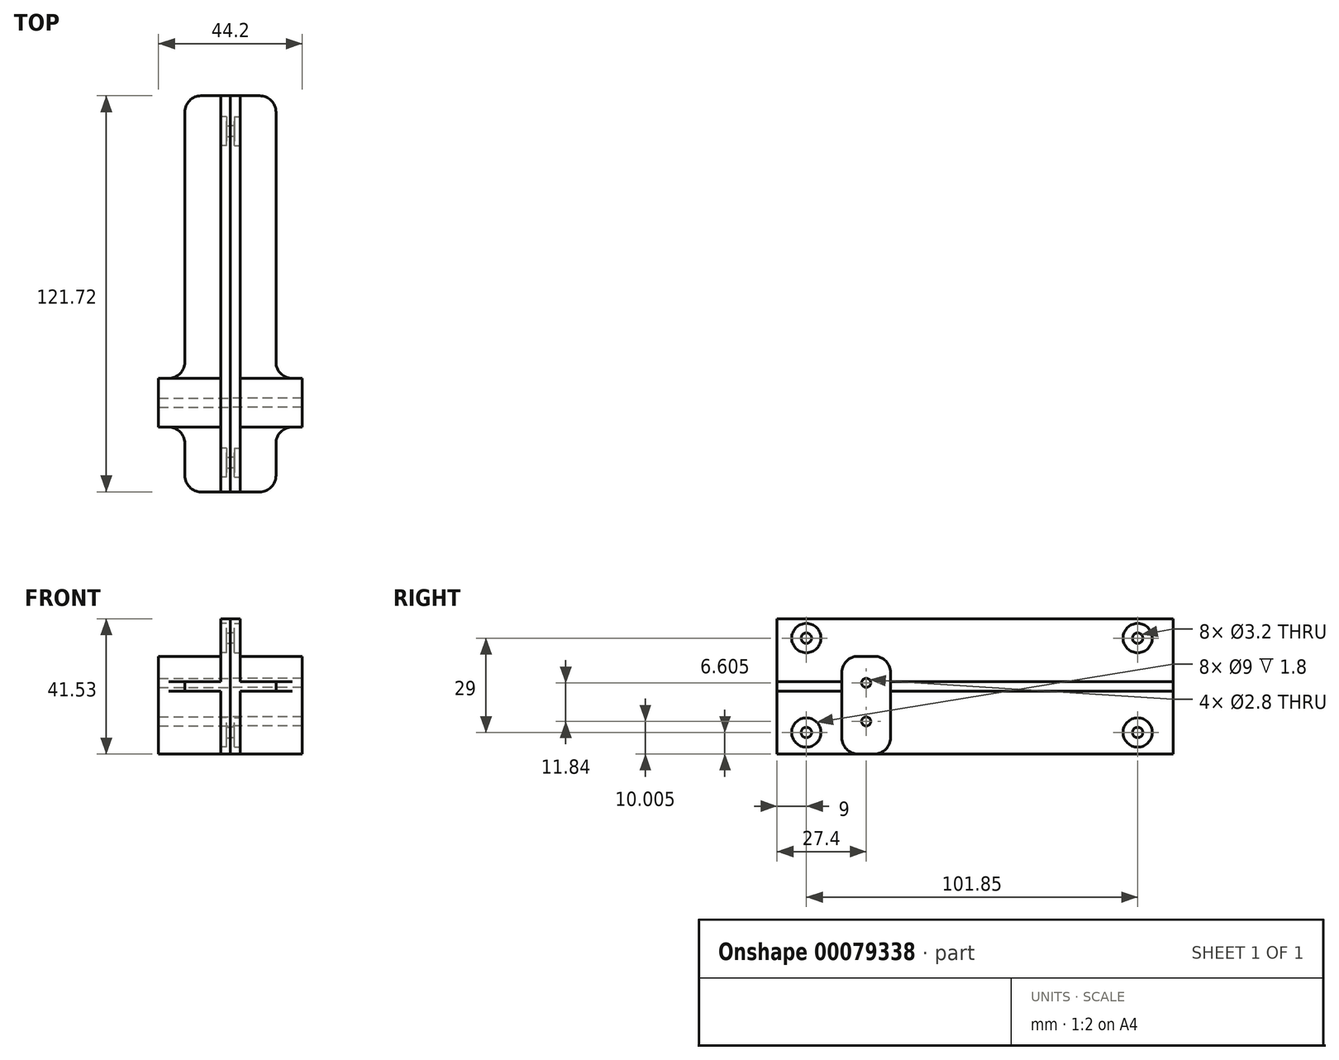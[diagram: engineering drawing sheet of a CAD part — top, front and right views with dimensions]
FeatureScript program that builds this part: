
annotation { "Feature Type Name" : "Feature", "Feature Type Description" : "" }
export const myFeature = defineFeature(function(context is Context, id is Id, definition is map)
    precondition{}
    {
        {
            var Q0;
            Q0=qCreatedBy(makeId("Right.planeOp"),FACE);
            var sketch = newSketch(context, id + "F0", { "sketchPlane" : qUnion([Q0])});
            skLineSegment(sketch, "E0.bottom", {"start": v(-83.36, 20.77) * mm, "end": v(83.36, 20.77) * mm});
            skLineSegment(sketch, "E0.top", {"start": v(-83.36, -20.76) * mm, "end": v(83.36, -20.76) * mm});
            skLineSegment(sketch, "E0.left", {"start": v(-83.36, 20.77) * mm, "end": v(-83.36, -20.76) * mm});
            skLineSegment(sketch, "E0.right", {"start": v(83.36, 20.77) * mm, "end": v(83.36, -20.76) * mm});
            skPoint(sketch, "E0.middle", {"position": v(0, 0) * mm});
            skLineSegment(sketch, "E1", {"start": v(-83.36, -10.77) * mm, "end": v(-35.96, -10.77) * mm, "construction": true});
            skLineSegment(sketch, "E2", {"start": v(-35.96, -10.76) * mm, "end": v(-35.96, -20.76) * mm, "construction": true});
            skLineSegment(sketch, "E3", {"start": v(-35.96, -10.77) * mm, "end": v(43.29, -10.77) * mm, "construction": true});
            skLineSegment(sketch, "E4", {"start": v(-35.96, -20.76) * mm, "end": v(-35.96, 1.08) * mm, "construction": true});
            skCircle(sketch, "E5", {"center": v(-35.96, -10.77) * mm, "radius": 1.4 * mm});
            skCircle(sketch, "E6", {"center": v(43.29, -10.77) * mm, "radius": 1.4 * mm});
            skCircle(sketch, "E7", {"center": v(-35.96, 1.08) * mm, "radius": 1.4 * mm});
            skLineSegment(sketch, "E8", {"start": v(-83.36, -14.16) * mm, "end": v(-54.36, -14.16) * mm, "construction": true});
            skLineSegment(sketch, "E9", {"start": v(-54.36, -14.16) * mm, "end": v(-54.36, -20.76) * mm, "construction": true});
            skLineSegment(sketch, "E10", {"start": v(-54.36, -14.16) * mm, "end": v(47.49, -14.16) * mm, "construction": true});
            skCircle(sketch, "E11", {"center": v(47.49, -14.16) * mm, "radius": 1.6 * mm});
            skCircle(sketch, "E12", {"center": v(-54.36, -14.16) * mm, "radius": 1.6 * mm});
            skLineSegment(sketch, "E13.bottom", {"start": v(-28.46, -20.76) * mm, "end": v(-43.46, -20.76) * mm});
            skLineSegment(sketch, "E13.left", {"start": v(-28.46, -20.76) * mm, "end": v(-28.46, 9.23) * mm});
            skLineSegment(sketch, "E13.right", {"start": v(-43.46, -20.76) * mm, "end": v(-43.46, 9.23) * mm});
            skLineSegment(sketch, "E14", {"start": v(-43.46, 9.23) * mm, "end": v(-28.46, 9.23) * mm});
            skLineSegment(sketch, "E15", {"start": v(-28.46, -5.76) * mm, "end": v(53.54, -5.76) * mm});
            skPoint(sketch, "E15.endSnap0", {"position": v(-28.46, -5.76) * mm});
            skLineSegment(sketch, "E16", {"start": v(53.54, -5.76) * mm, "end": v(53.54, -20.76) * mm});
            skLineSegment(sketch, "E17", {"start": v(-54.36, -14.16) * mm, "end": v(-54.36, 14.84) * mm, "construction": true});
            skLineSegment(sketch, "E18", {"start": v(-54.36, 14.84) * mm, "end": v(47.49, 14.84) * mm, "construction": true});
            skLineSegment(sketch, "E19", {"start": v(47.49, 14.84) * mm, "end": v(47.49, -14.16) * mm, "construction": true});
            skCircle(sketch, "E20", {"center": v(-54.36, 14.84) * mm, "radius": 1.6 * mm});
            skCircle(sketch, "E21", {"center": v(47.49, 14.84) * mm, "radius": 1.6 * mm});
            skSolve(sketch);
        }
        {
            var Q0;
            Q0=makeQuery(id+"F0.imprint","IMPRINT",FACE,{"disambiguationData":[TD([[makeQuery(id+"F0.imprint","IMPRINT",EDGE,{"derivedFrom":sQuery(id+"F0.wireOp",EDGE,"E0.bottom")}),-1.0]])]});
            var Q1;
            Q1=makeQuery(id+"F0.imprint","IMPRINT",FACE,{"disambiguationData":[TD([[makeQuery(id+"F0.imprint","IMPRINT",EDGE,{"derivedFrom":sQuery(id+"F0.wireOp",EDGE,"E6")}),-1.0]])]});
            var Q2;
            Q2=makeQuery(id+"F0.imprint","IMPRINT",FACE,{"disambiguationData":[TD([[makeQuery(id+"F0.imprint","IMPRINT",EDGE,{"derivedFrom":sQuery(id+"F0.wireOp",EDGE,"E6")}),1.0]])]});
            extrude(context, id + "F1", {"entities" : qUnion([Q0, Q1, Q2]), "depth" : 3 * mm});
        }
        {
            var Q0;
            Q0=makeQuery(id+"F0.imprint","IMPRINT",FACE,{"disambiguationData":[TD([[makeQuery(id+"F0.imprint","IMPRINT",EDGE,{"derivedFrom":sQuery(id+"F0.wireOp",EDGE,"E5")}),-1.0]])]});
            extrude(context, id + "F2", {"entities" : qUnion([Q0]), "operationType" : NewBodyOperationType.ADD, "depth" : 22.1 * mm});
        }
        {
            var Q0;
            Q0=makeQuery(id+"F2.opExtrude","SWEPT_EDGE",EDGE,{"disambiguationData":[OSD([sQuery(id+"F0.wireOp",EDGE,"E13.right"),sQuery(id+"F0.wireOp",EDGE,"E14")])]});
            var Q1;
            Q1=makeQuery(id+"F2.opExtrude","SWEPT_EDGE",EDGE,{"disambiguationData":[OSD([sQuery(id+"F0.wireOp",EDGE,"E13.left"),sQuery(id+"F0.wireOp",EDGE,"E14")])]});
            var Q2;
            Q2=makeQuery(id+"F2.opExtrude","SWEPT_EDGE",EDGE,{"disambiguationData":[OSD([sQuery(id+"F0.wireOp",EDGE,"E0.top"),sQuery(id+"F0.wireOp",EDGE,"E13.bottom"),sQuery(id+"F0.wireOp",EDGE,"E13.left")])]});
            var Q3;
            Q3=makeQuery(id+"F2.opExtrude","SWEPT_EDGE",EDGE,{"disambiguationData":[OSD([sQuery(id+"F0.wireOp",EDGE,"E0.top"),sQuery(id+"F0.wireOp",EDGE,"E13.bottom"),sQuery(id+"F0.wireOp",EDGE,"E13.right")])]});
            fillet(context, id + "F3", {"entities" : qUnion([Q0, Q1, Q2, Q3]), "radius" : 5 * mm, "tangentPropagation" : true, "allowEdgeOverflow" : false});
        }
        {
            var Q0;
            Q0=makeQuery(id+"F1.opExtrude","SWEPT_FACE",FACE,{"disambiguationData":[OSD([sQuery(id+"F0.wireOp",EDGE,"E0.left")])]});
            extrude(context, id + "F4", {"entities" : qUnion([Q0]), "operationType" : NewBodyOperationType.REMOVE, "oppositeDirection" : true, "depth" : 20 * mm});
        }
        {
            var Q0;
            Q0=makeQuery(id+"F1.opExtrude","SWEPT_FACE",FACE,{"disambiguationData":[OSD([sQuery(id+"F0.wireOp",EDGE,"E0.right")])]});
            extrude(context, id + "F5", {"entities" : qUnion([Q0]), "operationType" : NewBodyOperationType.REMOVE, "oppositeDirection" : true, "depth" : 25 * mm});
        }
        {
            var Q0;
            Q0=makeQuery(id+"F4.boolean.opBoolean","COPY",FACE,{"derivedFrom":makeQuery(id+"F4.opExtrude","CAP_FACE",FACE,{"disambiguationData":[OSD([sQuery(id+"F0.wireOp",EDGE,"E0.left")])],"isStart":false})});
            var sketch = newSketch(context, id + "F6", { "sketchPlane" : qUnion([Q0])});
            skLineSegment(sketch, "E22", {"start": v(3, 0) * mm, "end": v(3, 1.5) * mm});
            skLineSegment(sketch, "E23", {"start": v(3, 1.5) * mm, "end": v(14, 1.5) * mm});
            skLineSegment(sketch, "E24", {"start": v(14, 1.5) * mm, "end": v(14, -1.5) * mm});
            skLineSegment(sketch, "E25", {"start": v(14, -1.5) * mm, "end": v(3, -1.5) * mm});
            skLineSegment(sketch, "E26", {"start": v(3, -1.5) * mm, "end": v(3, 0) * mm});
            skSolve(sketch);
        }
        {
            var Q0;
            Q0=makeQuery(id+"F6.imprint","IMPRINT",FACE,{"disambiguationData":[TD([[makeQuery(id+"F6.imprint","IMPRINT",EDGE,{"derivedFrom":sQuery(id+"F6.wireOp",EDGE,"E22")}),1.0]])]});
            var Q1;
            Q1=makeQuery(id+"F5.boolean.opBoolean","COPY",FACE,{"derivedFrom":makeQuery(id+"F5.opExtrude","CAP_FACE",FACE,{"disambiguationData":[OSD([sQuery(id+"F0.wireOp",EDGE,"E0.right")])],"isStart":false})});
            extrude(context, id + "F7", {"entities" : qUnion([Q0]), "operationType" : NewBodyOperationType.ADD, "endBound" : BoundingType.UP_TO_SURFACE, "oppositeDirection" : true, "endBoundEntityFace" : qUnion([Q1]), "depth" : 25 * mm});
        }
        {
            var Q0;
            Q0=makeQuery(id+"F4.boolean.opBoolean","COPY",EDGE,{"derivedFrom":makeQuery(id+"F4.opExtrude","CAP_EDGE",EDGE,{"disambiguationData":[OSD([sQuery(id+"F0.wireOp",EDGE,"E0.top"),sQuery(id+"F0.wireOp",EDGE,"E0.left")])],"isStart":false})});
            var Q1;
            Q1=makeQuery(id+"F5.boolean.opBoolean","COPY",EDGE,{"derivedFrom":makeQuery(id+"F5.opExtrude","CAP_EDGE",EDGE,{"disambiguationData":[OSD([sQuery(id+"F0.wireOp",EDGE,"E0.top"),sQuery(id+"F0.wireOp",EDGE,"E0.right")])],"isStart":false})});
            var Q2;
            Q2=makeQuery(id+"F7.opExtrude","CAP_EDGE",EDGE,{"disambiguationData":[OSD([sQuery(id+"F6.wireOp",EDGE,"E24")])],"isStart":false});
            var Q3;
            Q3=makeQuery(id+"F7.boolean.opBoolean","INTERSECT",EDGE,{"derivedFrom":[makeQuery(id+"F2.opExtrude","SWEPT_FACE",FACE,{"disambiguationData":[OSD([sQuery(id+"F0.wireOp",EDGE,"E13.left")])]}),makeQuery(id+"F7.opExtrude","SWEPT_FACE",FACE,{"disambiguationData":[OSD([sQuery(id+"F6.wireOp",EDGE,"E24")])]})]});
            var Q4;
            Q4=makeQuery(id+"F7.boolean.opBoolean","INTERSECT",EDGE,{"derivedFrom":[makeQuery(id+"F2.opExtrude","SWEPT_FACE",FACE,{"disambiguationData":[OSD([sQuery(id+"F0.wireOp",EDGE,"E13.right")])]}),makeQuery(id+"F7.opExtrude","SWEPT_FACE",FACE,{"disambiguationData":[OSD([sQuery(id+"F6.wireOp",EDGE,"E24")])]})]});
            var Q5;
            Q5=makeQuery(id+"F7.opExtrude","CAP_EDGE",EDGE,{"disambiguationData":[OSD([sQuery(id+"F6.wireOp",EDGE,"E24")])],"isStart":true});
            var Q6;
            Q6=makeQuery(id+"F4.boolean.opBoolean","COPY",EDGE,{"derivedFrom":makeQuery(id+"F4.opExtrude","CAP_EDGE",EDGE,{"disambiguationData":[OSD([sQuery(id+"F0.wireOp",EDGE,"E0.bottom"),sQuery(id+"F0.wireOp",EDGE,"E0.left")])],"isStart":false})});
            var Q7;
            Q7=makeQuery(id+"F5.boolean.opBoolean","COPY",EDGE,{"derivedFrom":makeQuery(id+"F5.opExtrude","CAP_EDGE",EDGE,{"disambiguationData":[OSD([sQuery(id+"F0.wireOp",EDGE,"E0.bottom"),sQuery(id+"F0.wireOp",EDGE,"E0.right")])],"isStart":false})});
            fillet(context, id + "F8", {"entities" : qUnion([Q0, Q1, Q2, Q3, Q4, Q5, Q6, Q7]), "radius" : 5 * mm, "tangentPropagation" : true, "allowEdgeOverflow" : false});
        }
        {
            var Q0;
            {var subQ2=sQuery(id+"F0.wireOp",EDGE,"E11");var subQ3=sQuery(id+"F0.wireOp",EDGE,"E0.right");var subQ4=sQuery(id+"F0.wireOp",EDGE,"E0.top");var subQ6=sQuery(id+"F0.wireOp",EDGE,"E13.left");var subQ7=sQuery(id+"F0.wireOp",EDGE,"E0.left");var subQ8=sQuery(id+"F0.wireOp",EDGE,"E13.right");Q0=makeQuery(id+"F7.boolean.opBoolean","SPLIT",FACE,{"disambiguationData":[TD([makeQuery(id+"F1.opExtrude","SWEPT_FACE",FACE,{"disambiguationData":[OSD([subQ2])]})])],"derivedFrom":makeQuery(id+"F1.opExtrude","CAP_FACE",FACE,{"disambiguationData":[OSD([sQuery(id+"F0.wireOp",EDGE,"E0.bottom"),subQ4,subQ7,subQ3,subQ2,sQuery(id+"F0.wireOp",EDGE,"E12"),subQ6,subQ8,sQuery(id+"F0.wireOp",EDGE,"E14"),sQuery(id+"F0.wireOp",EDGE,"E20"),sQuery(id+"F0.wireOp",EDGE,"E21")])],"isStart":false})});}
            var sketch = newSketch(context, id + "F9", { "sketchPlane" : qUnion([Q0])});
            skCircle(sketch, "E27", {"center": v(-54.36, -14.16) * mm, "radius": 4.5 * mm});
            skCircle(sketch, "E28", {"center": v(47.49, -14.16) * mm, "radius": 4.5 * mm});
            skCircle(sketch, "E29", {"center": v(-54.36, 14.84) * mm, "radius": 4.5 * mm});
            skCircle(sketch, "E30", {"center": v(47.49, 14.84) * mm, "radius": 4.5 * mm});
            skSolve(sketch);
        }
        {
            var Q0;
            Q0=makeQuery(id+"F9.imprint","IMPRINT",FACE,{"disambiguationData":[TD([[makeQuery(id+"F9.imprint","IMPRINT",EDGE,{"derivedFrom":sQuery(id+"F9.wireOp",EDGE,"E27")}),1.0]])]});
            var Q1;
            Q1=makeQuery(id+"F9.imprint","IMPRINT",FACE,{"disambiguationData":[TD([[makeQuery(id+"F9.imprint","IMPRINT",EDGE,{"derivedFrom":sQuery(id+"F9.wireOp",EDGE,"E28")}),1.0]])]});
            var Q2;
            Q2=makeQuery(id+"F9.imprint","IMPRINT",FACE,{"disambiguationData":[TD([[makeQuery(id+"F9.imprint","IMPRINT",EDGE,{"derivedFrom":sQuery(id+"F9.wireOp",EDGE,"E29")}),1.0]])]});
            var Q3;
            Q3=makeQuery(id+"F9.imprint","IMPRINT",FACE,{"disambiguationData":[TD([[makeQuery(id+"F9.imprint","IMPRINT",EDGE,{"derivedFrom":sQuery(id+"F9.wireOp",EDGE,"E30")}),1.0]])]});
            extrude(context, id + "F10", {"entities" : qUnion([Q0, Q1, Q2, Q3]), "operationType" : NewBodyOperationType.REMOVE, "oppositeDirection" : true, "depth" : 1.8 * mm});
        }
        {
            var Q0;
            Q0=makeQuery(id+"F7.boolean.opBoolean","SPLIT",FACE,{"disambiguationData":[TD([makeQuery(id+"F2.opExtrude","SWEPT_FACE",FACE,{"disambiguationData":[OSD([sQuery(id+"F0.wireOp",EDGE,"E7")])]})])],"derivedFrom":makeQuery(id+"F7.opExtrude","SWEPT_FACE",FACE,{"disambiguationData":[OSD([sQuery(id+"F6.wireOp",EDGE,"E24")])]})});
            extrude(context, id + "F11", {"entities" : qUnion([Q0]), "operationType" : NewBodyOperationType.REMOVE, "endBound" : BoundingType.THROUGH_ALL, "oppositeDirection" : true, "depth" : 25 * mm});
        }
        {
            var Q0;
            Q0=makeQuery(id+"F1.opExtrude","SWEPT_BODY",BODY,{"disambiguationData":[OSD([sQuery(id+"F0.wireOp",EDGE,"E0.bottom"),sQuery(id+"F0.wireOp",EDGE,"E0.top"),sQuery(id+"F0.wireOp",EDGE,"E0.left"),sQuery(id+"F0.wireOp",EDGE,"E0.right"),sQuery(id+"F0.wireOp",EDGE,"E11"),sQuery(id+"F0.wireOp",EDGE,"E12"),sQuery(id+"F0.wireOp",EDGE,"E13.left"),sQuery(id+"F0.wireOp",EDGE,"E13.right"),sQuery(id+"F0.wireOp",EDGE,"E14")])]});
            var Q1;
            Q1=qCreatedBy(makeId("Right.planeOp"),FACE);
            mirror(context, id + "F12", {"entities" : qUnion([Q0]), "mirrorPlane" : qUnion([Q1])});
        }
    });
